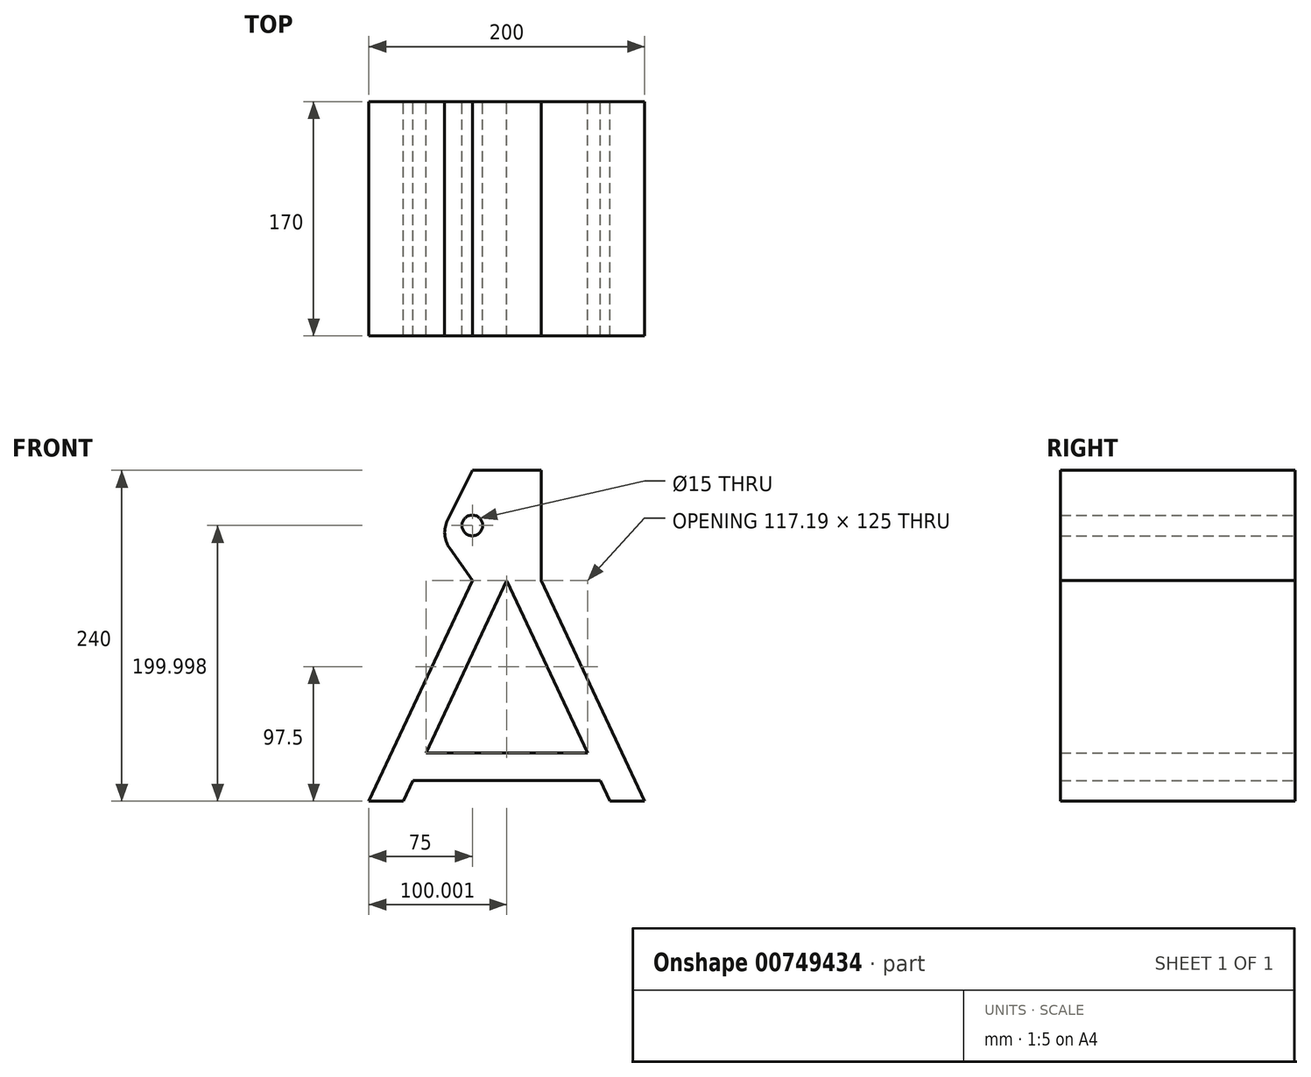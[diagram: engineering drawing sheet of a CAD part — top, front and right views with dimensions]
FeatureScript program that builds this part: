
annotation { "Feature Type Name" : "Feature", "Feature Type Description" : "" }
export const myFeature = defineFeature(function(context is Context, id is Id, definition is map)
    precondition{}
    {
        {
            var Q0;
            Q0=qCreatedBy(makeId("Front.planeOp"),FACE);
            var sketch = newSketch(context, id + "F0", { "sketchPlane" : qUnion([Q0])});
            skLineSegment(sketch, "E0", {"start": v(10.3, 40.36) * mm, "end": v(10.3, 120.36) * mm});
            skLineSegment(sketch, "E1", {"start": v(10.3, 120.36) * mm, "end": v(-39.7, 120.36) * mm});
            skArc(sketch, "E2", {"start": v(-57.61, 84.25) * mm, "mid": v(-59.64, 73.88) * mm, "end": v(-56.11, 63.93) * mm});
            skLineSegment(sketch, "E3", {"start": v(-57.61, 84.25) * mm, "end": v(-39.7, 120.36) * mm});
            skLineSegment(sketch, "E4", {"start": v(-39.7, 40.36) * mm, "end": v(-56.11, 63.93) * mm});
            skCircle(sketch, "E5", {"center": v(-39.7, 80.36) * mm, "radius": 7.5 * mm});
            skLineSegment(sketch, "E6", {"start": v(-14.7, 40.36) * mm, "end": v(10.3, 40.36) * mm});
            skLineSegment(sketch, "E7", {"start": v(-14.7, 40.36) * mm, "end": v(-39.7, 40.36) * mm});
            skLineSegment(sketch, "E8", {"start": v(-14.7, 40.36) * mm, "end": v(-14.7, -119.64) * mm, "construction": true});
            skLineSegment(sketch, "E9", {"start": v(-14.7, -119.64) * mm, "end": v(85.3, -119.64) * mm, "construction": true});
            skLineSegment(sketch, "E10", {"start": v(-14.7, -119.64) * mm, "end": v(-114.7, -119.64) * mm, "construction": true});
            skLineSegment(sketch, "E11", {"start": v(-39.7, 40.36) * mm, "end": v(-114.7, -119.64) * mm});
            skLineSegment(sketch, "E12", {"start": v(-89.7, -119.64) * mm, "end": v(-14.7, 40.36) * mm});
            skLineSegment(sketch, "E13", {"start": v(-14.7, 40.36) * mm, "end": v(60.3, -119.64) * mm});
            skLineSegment(sketch, "E14", {"start": v(10.3, 40.36) * mm, "end": v(85.3, -119.64) * mm});
            skLineSegment(sketch, "E15", {"start": v(-114.7, -119.64) * mm, "end": v(-89.7, -119.64) * mm});
            skLineSegment(sketch, "E16", {"start": v(60.3, -119.64) * mm, "end": v(85.3, -119.64) * mm});
            skLineSegment(sketch, "E17", {"start": v(-82.67, -104.64) * mm, "end": v(53.27, -104.64) * mm});
            skLineSegment(sketch, "E18", {"start": v(-73.3, -84.64) * mm, "end": v(43.9, -84.64) * mm});
            skSolve(sketch);
        }
        {
            var Q0;
            Q0 = qSketchRegion(id + "F0", true);
            extrude(context, id + "F1", {"entities" : qUnion([Q0]), "depth" : 170 * mm, "offsetDistance" : 25 * mm});
        }
        {
            var Q0;
            Q0=makeQuery(id+"F1.opExtrude","SWEPT_FACE",FACE,{"disambiguationData":[OSD([sQuery(id+"F0.wireOp",EDGE,"E11")])]});
            var sketch = newSketch(context, id + "F2", { "sketchPlane" : qUnion([Q0])});
            skLineSegment(sketch, "E19", {"start": v(0, -157.01) * mm, "end": v(63.22, 19.7) * mm});
            skLineSegment(sketch, "E20", {"start": v(170, -157.01) * mm, "end": v(97.9, 19.7) * mm});
            skLineSegment(sketch, "E21", {"start": v(25, -157.01) * mm, "end": v(0, -157.01) * mm});
            skLineSegment(sketch, "E22", {"start": v(145, -157.01) * mm, "end": v(170, -157.01) * mm});
            skLineSegment(sketch, "E23", {"start": v(81.07, 19.7) * mm, "end": v(81.07, -0.3) * mm});
            skLineSegment(sketch, "E24", {"start": v(25, -157.01) * mm, "end": v(81.07, -0.3) * mm});
            skLineSegment(sketch, "E25", {"start": v(81.07, -0.3) * mm, "end": v(145, -157.01) * mm});
            skLineSegment(sketch, "E26", {"start": v(37.52, -122.01) * mm, "end": v(130.72, -122.01) * mm});
            skLineSegment(sketch, "E27", {"start": v(30.37, -142.01) * mm, "end": v(138.88, -142.01) * mm});
            skLineSegment(sketch, "E28", {"start": v(81.07, -0.3) * mm, "end": v(56.07, -0.3) * mm, "construction": true});
            skLineSegment(sketch, "E29", {"start": v(81.07, -0.3) * mm, "end": v(106.07, -0.3) * mm, "construction": true});
            skSolve(sketch);
        }
    });
